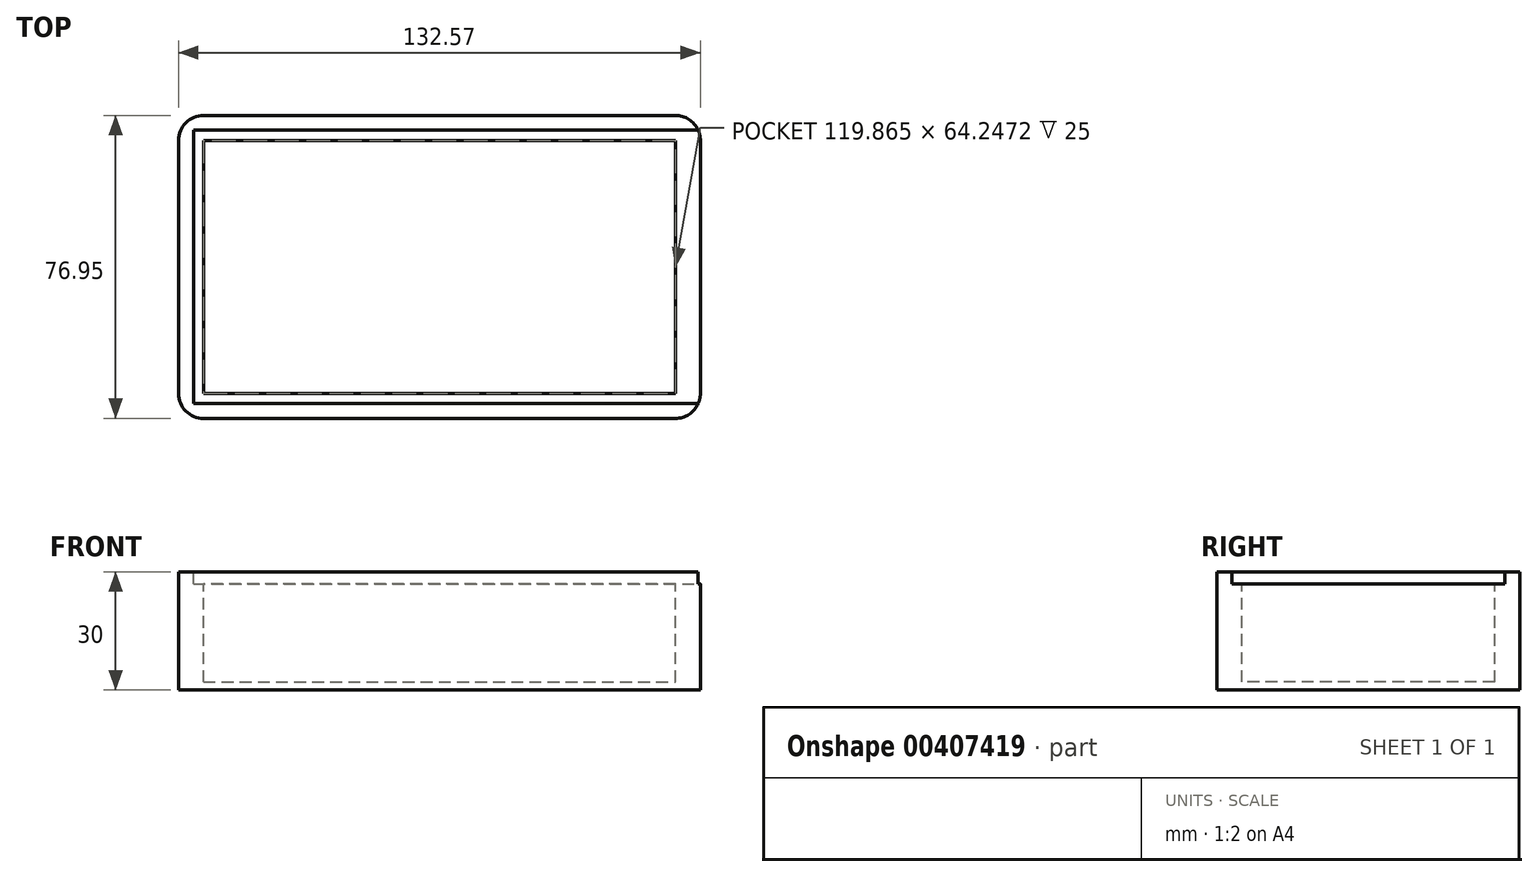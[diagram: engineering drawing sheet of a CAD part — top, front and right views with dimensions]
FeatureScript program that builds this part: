
annotation { "Feature Type Name" : "Feature", "Feature Type Description" : "" }
export const myFeature = defineFeature(function(context is Context, id is Id, definition is map)
    precondition{}
    {
        {
            var Q0;
            Q0=qCreatedBy(makeId("Top.planeOp"),FACE);
            var sketch = newSketch(context, id + "F0", { "sketchPlane" : qUnion([Q0])});
            skLineSegment(sketch, "E0.bottom", {"start": v(-6.35, 0) * mm, "end": v(-126.22, 0) * mm});
            skLineSegment(sketch, "E0.top", {"start": v(-6.35, -76.95) * mm, "end": v(-126.22, -76.95) * mm});
            skLineSegment(sketch, "E0.left", {"start": v(0, -6.35) * mm, "end": v(0, -70.6) * mm});
            skLineSegment(sketch, "E0.right", {"start": v(-132.57, -6.35) * mm, "end": v(-132.57, -70.6) * mm});
            skPoint(sketch, "E1.visualSharp", {"position": v(-132.57, 0) * mm});
            skArc(sketch, "E1.filletArc", {"start": v(-126.22, 0) * mm, "mid": v(-130.7, -1.86) * mm, "end": v(-132.57, -6.35) * mm});
            skPoint(sketch, "E2.visualSharp", {"position": v(-132.57, -76.95) * mm});
            skArc(sketch, "E2.filletArc", {"start": v(-132.57, -70.6) * mm, "mid": v(-130.7, -75.09) * mm, "end": v(-126.22, -76.95) * mm});
            skPoint(sketch, "E3.visualSharp", {"position": v(0, 0) * mm});
            skArc(sketch, "E3.filletArc", {"start": v(0, -6.35) * mm, "mid": v(-1.86, -1.86) * mm, "end": v(-6.35, 0) * mm});
            skPoint(sketch, "E4.visualSharp", {"position": v(0, -76.95) * mm});
            skArc(sketch, "E4.filletArc", {"start": v(-6.35, -76.95) * mm, "mid": v(-1.86, -75.09) * mm, "end": v(0, -70.6) * mm});
            skSolve(sketch);
        }
        {
            var Q0;
            Q0=makeQuery(id+"F0.imprint","IMPRINT",FACE,{"disambiguationData":[TD([[makeQuery(id+"F0.imprint","IMPRINT",EDGE,{"derivedFrom":sQuery(id+"F0.wireOp",EDGE,"E0.bottom")}),1.0]])]});
            extrude(context, id + "F1", {"entities" : qUnion([Q0]), "depth" : 30 * mm});
        }
        {
            var Q0;
            Q0=makeQuery(id+"F1.opExtrude","CAP_FACE",FACE,{"disambiguationData":[OSD([sQuery(id+"F0.wireOp",EDGE,"E0.bottom"),sQuery(id+"F0.wireOp",EDGE,"E0.top"),sQuery(id+"F0.wireOp",EDGE,"E0.left"),sQuery(id+"F0.wireOp",EDGE,"E0.right"),sQuery(id+"F0.wireOp",EDGE,"E1.filletArc"),sQuery(id+"F0.wireOp",EDGE,"E2.filletArc"),sQuery(id+"F0.wireOp",EDGE,"E3.filletArc"),sQuery(id+"F0.wireOp",EDGE,"E4.filletArc")])],"isStart":false});
            var sketch = newSketch(context, id + "F2", { "sketchPlane" : qUnion([Q0])});
            skLineSegment(sketch, "E5.bottom", {"start": v(-126.22, -6.35) * mm, "end": v(-6.35, -6.35) * mm});
            skLineSegment(sketch, "E5.top", {"start": v(-126.22, -70.6) * mm, "end": v(-6.35, -70.6) * mm});
            skLineSegment(sketch, "E5.left", {"start": v(-126.22, -6.35) * mm, "end": v(-126.22, -70.6) * mm});
            skLineSegment(sketch, "E5.right", {"start": v(-6.35, -6.35) * mm, "end": v(-6.35, -70.6) * mm});
            skSolve(sketch);
        }
        {
            var Q0;
            Q0=qSketchRegion(id+"F2",true);
            extrude(context, id + "F3", {"entities" : qUnion([Q0]), "operationType" : NewBodyOperationType.REMOVE, "oppositeDirection" : true, "depth" : 28 * mm});
        }
        {
            var Q0;
            Q0=makeQuery(id+"F1.opExtrude","CAP_FACE",FACE,{"disambiguationData":[OSD([sQuery(id+"F0.wireOp",EDGE,"E0.bottom"),sQuery(id+"F0.wireOp",EDGE,"E0.top"),sQuery(id+"F0.wireOp",EDGE,"E0.left"),sQuery(id+"F0.wireOp",EDGE,"E0.right"),sQuery(id+"F0.wireOp",EDGE,"E1.filletArc"),sQuery(id+"F0.wireOp",EDGE,"E2.filletArc"),sQuery(id+"F0.wireOp",EDGE,"E3.filletArc"),sQuery(id+"F0.wireOp",EDGE,"E4.filletArc")])],"isStart":false});
            var sketch = newSketch(context, id + "F4", { "sketchPlane" : qUnion([Q0])});
            skLineSegment(sketch, "E6.bottom", {"start": v(-128.77, -3.72) * mm, "end": v(7.8, -3.72) * mm});
            skLineSegment(sketch, "E6.top", {"start": v(-128.77, -73.16) * mm, "end": v(7.8, -73.16) * mm});
            skLineSegment(sketch, "E6.left", {"start": v(-128.77, -3.72) * mm, "end": v(-128.77, -73.16) * mm});
            skLineSegment(sketch, "E6.right", {"start": v(7.8, -3.72) * mm, "end": v(7.8, -73.16) * mm});
            skSolve(sketch);
        }
        {
            var Q0;
            Q0=qSketchRegion(id+"F4",true);
            extrude(context, id + "F5", {"entities" : qUnion([Q0]), "operationType" : NewBodyOperationType.REMOVE, "oppositeDirection" : true, "depth" : 3 * mm});
        }
    });
